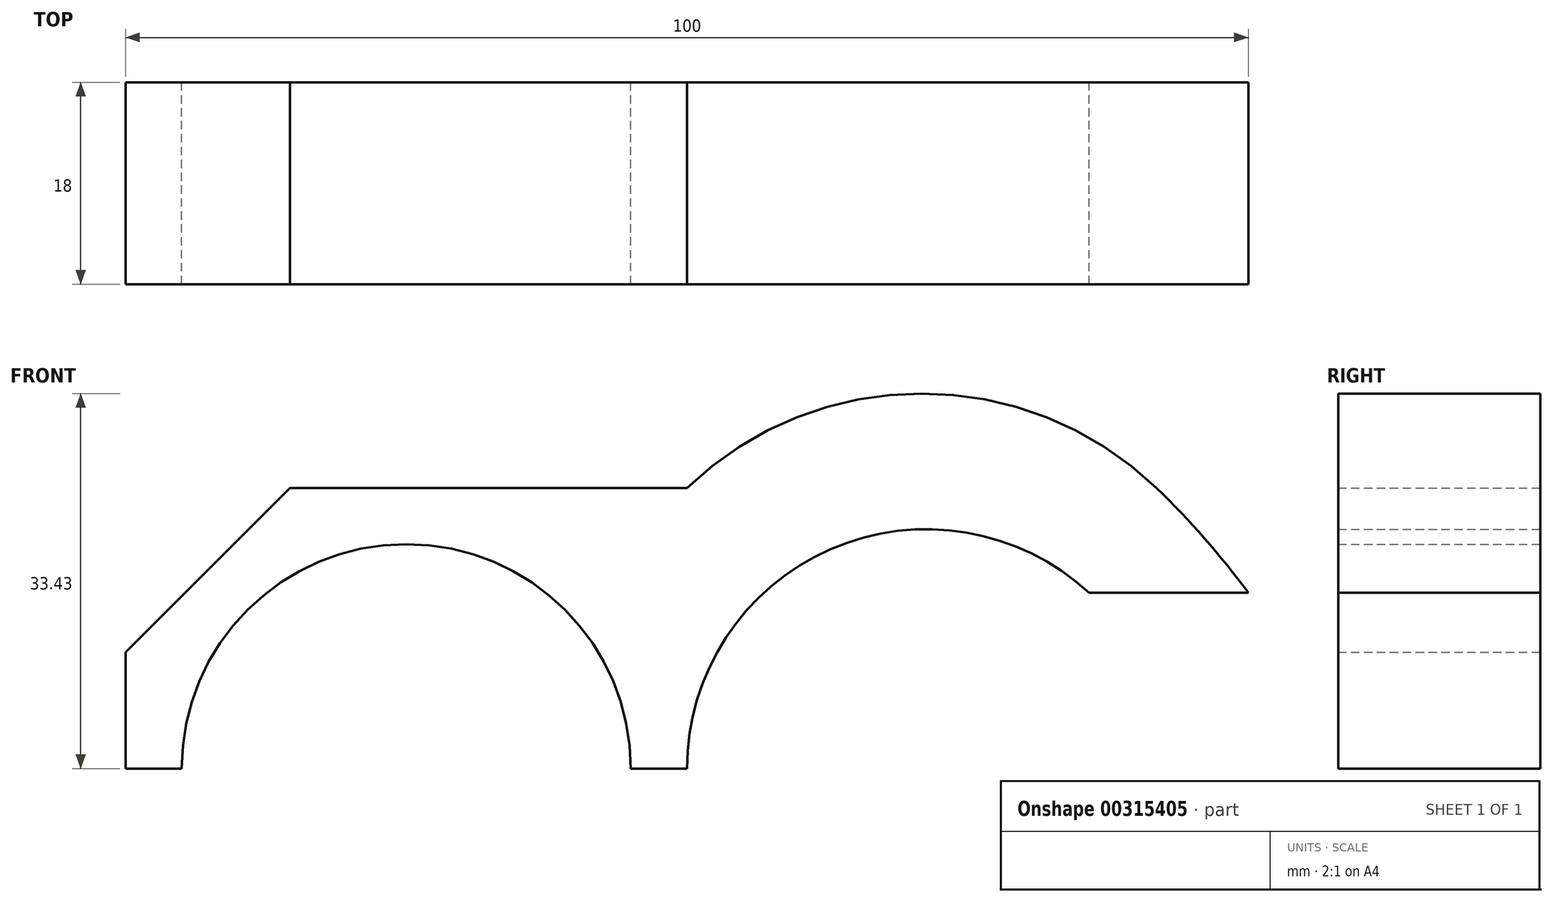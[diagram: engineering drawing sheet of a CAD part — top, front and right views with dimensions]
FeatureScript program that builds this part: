
annotation { "Feature Type Name" : "Feature", "Feature Type Description" : "" }
export const myFeature = defineFeature(function(context is Context, id is Id, definition is map)
    precondition{}
    {
        {
            var Q0;
            Q0=qCreatedBy(makeId("Front.planeOp"),FACE);
            var sketch = newSketch(context, id + "F0", { "sketchPlane" : qUnion([Q0])});
            skArc(sketch, "E0", {"start": v(-25, 0) * mm, "mid": v(-45, 20) * mm, "end": v(-65, 0) * mm});
            skCircle(sketch, "E1", {"center": v(0, 0) * mm, "radius": 20 * mm, "construction": true});
            skArc(sketch, "E2", {"start": v(-20, 0) * mm, "mid": v(-45, 25) * mm, "end": v(-70, 0) * mm, "construction": true});
            skLineSegment(sketch, "E3.bottom", {"start": v(-70, 0) * mm, "end": v(-65, 0) * mm});
            skLineSegment(sketch, "E3.left", {"start": v(-70, 0) * mm, "end": v(-70, 10.36) * mm});
            skLineSegment(sketch, "E3.right", {"start": v(0, 0) * mm, "end": v(0, 39.51) * mm});
            skPoint(sketch, "E4", {"position": v(-65, 0) * mm});
            skArc(sketch, "E5", {"start": v(15.8, 15.67) * mm, "mid": v(-7.22, 19.54) * mm, "end": v(-20, 0) * mm});
            skLineSegment(sketch, "E6", {"start": v(-20, 0) * mm, "end": v(-20, 25) * mm, "construction": true});
            skLineSegment(sketch, "E7.bottom", {"start": v(0, 0) * mm, "end": v(30, 0) * mm, "construction": true});
            skLineSegment(sketch, "E7.top", {"start": v(0, 35.69) * mm, "end": v(30, 35.69) * mm, "construction": true});
            skLineSegment(sketch, "E7.left", {"start": v(0, 0) * mm, "end": v(0, 21.3) * mm, "construction": true});
            skLineSegment(sketch, "E7.right", {"start": v(30, 0) * mm, "end": v(30, 35.69) * mm, "construction": true});
            skLineSegment(sketch, "E8", {"start": v(-20, 0) * mm, "end": v(-20, 0) * mm});
            skLineSegment(sketch, "E9.trimOffspring", {"start": v(-25, 0) * mm, "end": v(-20, 0) * mm});
            skLineSegment(sketch, "E10", {"start": v(-70, 10.36) * mm, "end": v(-55.36, 25) * mm});
            skLineSegment(sketch, "E11", {"start": v(-45, 25) * mm, "end": v(-20, 25) * mm});
            skLineSegment(sketch, "E12", {"start": v(-45, 25) * mm, "end": v(-55.36, 25) * mm});
            skLineSegment(sketch, "E13", {"start": v(15.8, 15.67) * mm, "end": v(30, 15.67) * mm});
            skArc(sketch, "E14", {"start": v(30, 15.67) * mm, "mid": v(26.1, 20.5) * mm, "end": v(21.82, 25) * mm});
            skArc(sketch, "E15", {"start": v(21.82, 25) * mm, "mid": v(0.91, 33.43) * mm, "end": v(-20, 25) * mm});
            skArc(sketch, "E16", {"start": v(21.82, 25) * mm, "mid": v(11.56, 33.24) * mm, "end": v(0, 39.51) * mm, "construction": true});
            skLineSegment(sketch, "E17", {"start": v(0, 21.3) * mm, "end": v(0, 35.69) * mm});
            skLineSegment(sketch, "E18", {"start": v(-20, 0) * mm, "end": v(0, 0) * mm, "construction": true});
            skSolve(sketch);
        }
        {
            var Q0;
            {var subQ8=sQuery(id+"F0.wireOp",EDGE,"E0");Q0=makeQuery(id+"F0.imprint","IMPRINT",FACE,{"disambiguationData":[TD([[makeQuery(id+"F0.imprint","IMPRINT",EDGE,{"derivedFrom":subQ8}),-1.0]])]});}
            var Q1;
            {var subQ4=sQuery(id+"F0.wireOp",EDGE,"E13");Q1=makeQuery(id+"F0.imprint","IMPRINT",FACE,{"disambiguationData":[TD([[makeQuery(id+"F0.imprint","IMPRINT",EDGE,{"derivedFrom":subQ4}),1.0]])]});}
            var Q2;
            Q2=sQuery(id+"F0.wireOp",EDGE,"E18");
            var Q3;
            Q3=sQuery(id+"F0.wireOp",EDGE,"E0");
            var Q4;
            Q4=sQuery(id+"F0.wireOp",EDGE,"E12");
            var Q5;
            Q5=sQuery(id+"F0.wireOp",EDGE,"E10");
            var Q6;
            Q6=sQuery(id+"F0.wireOp",EDGE,"E3.left");
            var Q7;
            Q7=sQuery(id+"F0.wireOp",EDGE,"E3.bottom");
            extrude(context, id + "F1", {"entities" : qUnion([Q0, Q1]), "surfaceEntities" : qUnion([Q2, Q3, Q4, Q5, Q6, Q7]), "depth" : 18 * mm});
        }
    });
